# Revit family: QF_ADVENTYS_ADV1494-A_GL650FL
name_source: partatom
category: Attrezzature speciali
units: mm (PartAtom-declared; Revit-internal decimal feet)

## family parameters
Condiviso = No
Host = Superficie
Punto di calcolo locali = No
Quota connettore circolare = Usa diametro
Taglio con vuoti quando caricato = No
Tipo di parte = Normale

## types (1)
- ADV1494-A
    Cycle = 50 Hz
    Depth = 340 mm  [stored 1.11549 ft]
    Depth Actual = 340 mm  [stored 1.11549 ft]
    Depth_Cutout = 346 mm  [stored 1.13517 ft]
    Depth_Generator = 300 mm  [stored 0.984252 ft]
    EI_X = 49.5 mm  [stored 0.162402 ft]
    EI_Y = 51.5 mm  [stored 0.168963 ft]
    Height = 172 mm  [stored 0.564304 ft]
    Height Actual = 172 mm  [stored 0.564304 ft]
    Height_Generator = 93.1 mm  [stored 0.305446 ft]
    Item Number = ADV1494-A
    Length Actual = 340 mm  [stored 1.11549 ft]
    Modello = GL650FL
    Phase = 1
    Produttore = ADVENTYS
    Prospetto di default = 1219.2 mm  [stored 4 ft]
    URL = https://adventys.com
    Volts = 220 V
    Watts = 650 W
    Weight = 8
    Width = 340 mm  [stored 1.11549 ft]
    Width_Cutout = 346 mm  [stored 1.13517 ft]
    Width_Generator = 300 mm  [stored 0.984252 ft]

note: [stored X ft] marks values corroborated as IEEE doubles in the binary element streams (Revit-internal decimal feet)
